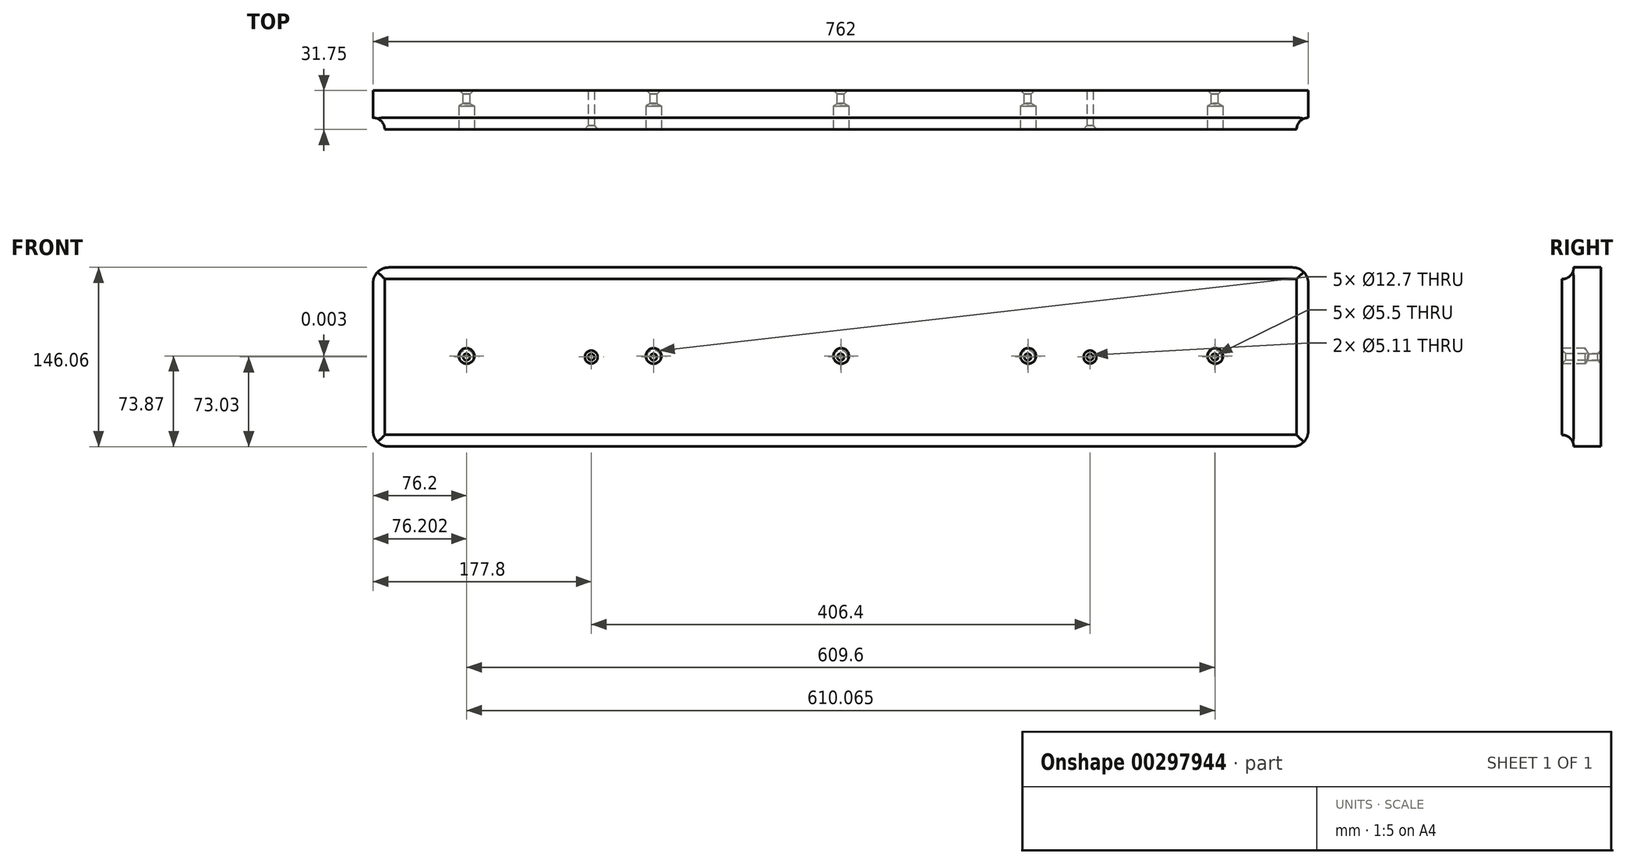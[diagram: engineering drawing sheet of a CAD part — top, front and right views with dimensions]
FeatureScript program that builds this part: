
annotation { "Feature Type Name" : "Feature", "Feature Type Description" : "" }
export const myFeature = defineFeature(function(context is Context, id is Id, definition is map)
    precondition{}
    {
        {
            var Q0;
            Q0=qCreatedBy(makeId("Front.planeOp"),FACE);
            var sketch = newSketch(context, id + "F0", { "sketchPlane" : qUnion([Q0])});
            skLineSegment(sketch, "E0.bottom", {"start": v(-381, 73.03) * mm, "end": v(381, 73.03) * mm});
            skLineSegment(sketch, "E0.top", {"start": v(-381, -73.03) * mm, "end": v(381, -73.03) * mm});
            skLineSegment(sketch, "E0.left", {"start": v(-381, 73.03) * mm, "end": v(-381, -73.03) * mm});
            skLineSegment(sketch, "E0.right", {"start": v(381, 73.03) * mm, "end": v(381, -73.03) * mm});
            skPoint(sketch, "E0.middle", {"position": v(0, 0) * mm});
            skLineSegment(sketch, "E1", {"start": v(0, 0) * mm, "end": v(152.4, 0) * mm, "construction": true});
            skLineSegment(sketch, "E2", {"start": v(152.4, 0) * mm, "end": v(304.8, 0) * mm, "construction": true});
            skLineSegment(sketch, "E3", {"start": v(0, 0) * mm, "end": v(-152.4, 0) * mm, "construction": true});
            skLineSegment(sketch, "E4", {"start": v(-152.4, 0) * mm, "end": v(-304.8, 0) * mm, "construction": true});
            skPoint(sketch, "E5", {"position": v(-304.8, 0) * mm});
            skPoint(sketch, "E6", {"position": v(-152.4, 0) * mm});
            skPoint(sketch, "E7", {"position": v(152.4, 0) * mm});
            skPoint(sketch, "E8", {"position": v(304.8, 0) * mm});
            skSolve(sketch);
        }
        {
            var Q0;
            Q0=qSketchRegion(id+"F0",true);
            extrude(context, id + "F1", {"entities" : qUnion([Q0]), "depth" : 31.75 * mm});
        }
        {
            var Q0;
            Q0=makeQuery(id+"F1.opExtrude","SWEPT_FACE",FACE,{"disambiguationData":[OSD([sQuery(id+"F0.wireOp",EDGE,"E0.left")])]});
            var sketch = newSketch(context, id + "F2", { "sketchPlane" : qUnion([Q0])});
            skCircle(sketch, "E9", {"center": v(31.75, 73.02) * mm, "radius": 9.53 * mm});
            skSolve(sketch);
        }
        {
            var Q0;
            Q0=qSketchRegion(id+"F2",true);
            extrude(context, id + "F3", {"entities" : qUnion([Q0]), "operationType" : NewBodyOperationType.REMOVE, "endBound" : BoundingType.THROUGH_ALL, "oppositeDirection" : true, "depth" : 25.4 * mm});
        }
        {
            var Q0;
            Q0=makeQuery(id+"F1.opExtrude","SWEPT_FACE",FACE,{"disambiguationData":[OSD([sQuery(id+"F0.wireOp",EDGE,"E0.bottom")])]});
            var sketch = newSketch(context, id + "F4", { "sketchPlane" : qUnion([Q0])});
            skCircle(sketch, "E10", {"center": v(-381, -31.73) * mm, "radius": 9.53 * mm});
            skSolve(sketch);
        }
        {
            var Q0;
            Q0=qSketchRegion(id+"F4",true);
            extrude(context, id + "F5", {"entities" : qUnion([Q0]), "operationType" : NewBodyOperationType.REMOVE, "endBound" : BoundingType.THROUGH_ALL, "oppositeDirection" : true, "depth" : 25.4 * mm});
        }
        {
            var Q0;
            Q0=makeQuery(id+"F1.opExtrude","SWEPT_FACE",FACE,{"disambiguationData":[OSD([sQuery(id+"F0.wireOp",EDGE,"E0.right")])]});
            var sketch = newSketch(context, id + "F6", { "sketchPlane" : qUnion([Q0])});
            skCircle(sketch, "E11", {"center": v(-31.75, -73.02) * mm, "radius": 9.53 * mm});
            skSolve(sketch);
        }
        {
            var Q0;
            Q0=qSketchRegion(id+"F6",true);
            extrude(context, id + "F7", {"entities" : qUnion([Q0]), "operationType" : NewBodyOperationType.REMOVE, "endBound" : BoundingType.THROUGH_ALL, "oppositeDirection" : true, "depth" : 25.4 * mm});
        }
        {
            var Q0;
            Q0=makeQuery(id+"F1.opExtrude","SWEPT_FACE",FACE,{"disambiguationData":[OSD([sQuery(id+"F0.wireOp",EDGE,"E0.top")])]});
            var sketch = newSketch(context, id + "F8", { "sketchPlane" : qUnion([Q0])});
            skCircle(sketch, "E12", {"center": v(381.03, 31.77) * mm, "radius": 9.52 * mm});
            skSolve(sketch);
        }
        {
            var Q0;
            Q0=qSketchRegion(id+"F8",true);
            extrude(context, id + "F9", {"entities" : qUnion([Q0]), "operationType" : NewBodyOperationType.REMOVE, "endBound" : BoundingType.THROUGH_ALL, "oppositeDirection" : true, "depth" : 25.4 * mm});
        }
        {
            var Q0;
            Q0=makeQuery(id+"F1.opExtrude","CAP_FACE",FACE,{"disambiguationData":[OSD([sQuery(id+"F0.wireOp",EDGE,"E0.bottom"),sQuery(id+"F0.wireOp",EDGE,"E0.top"),sQuery(id+"F0.wireOp",EDGE,"E0.left"),sQuery(id+"F0.wireOp",EDGE,"E0.right")])],"isStart":false});
            var sketch = newSketch(context, id + "F10", { "sketchPlane" : qUnion([Q0])});
            skLineSegment(sketch, "E13", {"start": v(0.47, 0.84) * mm, "end": v(152.87, 0.84) * mm, "construction": true});
            skLineSegment(sketch, "E14", {"start": v(152.87, 0.84) * mm, "end": v(305.27, 0.84) * mm, "construction": true});
            skLineSegment(sketch, "E15", {"start": v(-152.4, 0.84) * mm, "end": v(-304.8, 0.84) * mm, "construction": true});
            skLineSegment(sketch, "E16", {"start": v(0, 0) * mm, "end": v(-152.4, 0.84) * mm, "construction": true});
            skSolve(sketch);
        }
        {
            var Q0;
            Q0=sQuery(id+"F10.wireOp",VERTEX,"E15.end");
            var Q1;
            Q1=sQuery(id+"F10.wireOp",VERTEX,"E15.start");
            var Q2;
            Q2=sQuery(id+"F10.wireOp",VERTEX,"E13.start");
            var Q3;
            Q3=sQuery(id+"F10.wireOp",VERTEX,"E14.start");
            var Q4;
            Q4=sQuery(id+"F10.wireOp",VERTEX,"E14.end");
            var Q5;
            Q5=makeQuery(id+"F1.opExtrude","SWEPT_BODY",BODY,{"disambiguationData":[OSD([sQuery(id+"F0.wireOp",EDGE,"E0.bottom"),sQuery(id+"F0.wireOp",EDGE,"E0.top"),sQuery(id+"F0.wireOp",EDGE,"E0.left"),sQuery(id+"F0.wireOp",EDGE,"E0.right")])]});
            hole(context, id + "F11", {"style" : HoleStyle.SIMPLE, "endStyle" : HoleEndStyle.BLIND, "holeDiameter" : 12.7 * mm, "holeDepth" : 19.05 * mm, "tappedDepth" : 12.7 * mm, "tapClearance" : 3, "locations" : qUnion([Q0, Q1, Q2, Q3, Q4]), "scope" : qUnion([Q5])});
        }
        {
            var Q0;
            Q0=sQuery(id+"F0.wireOp",VERTEX,"E8");
            var Q1;
            Q1=sQuery(id+"F0.wireOp",VERTEX,"E7");
            var Q2;
            Q2=sQuery(id+"F0.wireOp",VERTEX,"E0.middle");
            var Q3;
            Q3=sQuery(id+"F0.wireOp",VERTEX,"E6");
            var Q4;
            Q4=sQuery(id+"F0.wireOp",VERTEX,"E5");
            var Q5;
            Q5=makeQuery(id+"F1.opExtrude","SWEPT_BODY",BODY,{"disambiguationData":[OSD([sQuery(id+"F0.wireOp",EDGE,"E0.bottom"),sQuery(id+"F0.wireOp",EDGE,"E0.top"),sQuery(id+"F0.wireOp",EDGE,"E0.left"),sQuery(id+"F0.wireOp",EDGE,"E0.right")])]});
            hole(context, id + "F12", {"style" : HoleStyle.C_SINK, "endStyle" : HoleEndStyle.THROUGH, "oppositeDirection" : true, "holeDiameter" : 5.5 * mm, "cSinkDiameter" : 11.2 * mm, "cSinkAngle" : 90 * degree, "tappedDepth" : 12.7 * mm, "tapClearance" : 3, "locations" : qUnion([Q0, Q1, Q2, Q3, Q4]), "scope" : qUnion([Q5])});
        }
        {
            var Q0;
            Q0=makeQuery(id+"F1.opExtrude","CAP_FACE",FACE,{"disambiguationData":[OSD([sQuery(id+"F0.wireOp",EDGE,"E0.bottom"),sQuery(id+"F0.wireOp",EDGE,"E0.top"),sQuery(id+"F0.wireOp",EDGE,"E0.left"),sQuery(id+"F0.wireOp",EDGE,"E0.right")])],"isStart":false});
            var sketch = newSketch(context, id + "F13", { "sketchPlane" : qUnion([Q0])});
            skLineSegment(sketch, "E17", {"start": v(0, 0) * mm, "end": v(-203.2, 0) * mm, "construction": true});
            skLineSegment(sketch, "E18", {"start": v(0, 0) * mm, "end": v(203.2, 0) * mm, "construction": true});
            skPoint(sketch, "E19", {"position": v(-203.2, 0) * mm});
            skPoint(sketch, "E20", {"position": v(203.2, 0) * mm});
            skSolve(sketch);
        }
        {
            var Q0;
            Q0=sQuery(id+"F13.wireOp",VERTEX,"E19");
            var Q1;
            Q1=sQuery(id+"F13.wireOp",VERTEX,"E18.end");
            var Q2;
            Q2=makeQuery(id+"F1.opExtrude","SWEPT_BODY",BODY,{"disambiguationData":[OSD([sQuery(id+"F0.wireOp",EDGE,"E0.bottom"),sQuery(id+"F0.wireOp",EDGE,"E0.top"),sQuery(id+"F0.wireOp",EDGE,"E0.left"),sQuery(id+"F0.wireOp",EDGE,"E0.right")])]});
            hole(context, id + "F14", {"style" : HoleStyle.C_SINK, "endStyle" : HoleEndStyle.THROUGH, "standardTappedOrClearance" : lookupTablePath({ "standard" : "ANSI", "fit" : "Normal (ASME)", "size" : "#10", "type" : "Clearance" }), "standardBlindInLast" : lookupTablePath({ "fit" : "Free", "standard" : "ANSI", "size" : "#10", "type" : "Clearance" }), "holeDiameter" : 5.1 * mm, "cSinkDiameter" : 10.44 * mm, "cSinkAngle" : 82 * degree, "tappedDepth" : 12.7 * mm, "tapClearance" : 3, "locations" : qUnion([Q0, Q1]), "scope" : qUnion([Q2])});
        }
        {
            var Q0;
            Q0=makeQuery(id+"F1.opExtrude","SWEPT_EDGE",EDGE,{"disambiguationData":[OSD([sQuery(id+"F0.wireOp",EDGE,"E0.bottom"),sQuery(id+"F0.wireOp",EDGE,"E0.right")])]});
            var Q1;
            Q1=makeQuery(id+"F1.opExtrude","SWEPT_EDGE",EDGE,{"disambiguationData":[OSD([sQuery(id+"F0.wireOp",EDGE,"E0.top"),sQuery(id+"F0.wireOp",EDGE,"E0.right")])]});
            var Q2;
            Q2=makeQuery(id+"F1.opExtrude","SWEPT_EDGE",EDGE,{"disambiguationData":[OSD([sQuery(id+"F0.wireOp",EDGE,"E0.bottom"),sQuery(id+"F0.wireOp",EDGE,"E0.left")])]});
            var Q3;
            Q3=makeQuery(id+"F1.opExtrude","SWEPT_EDGE",EDGE,{"disambiguationData":[OSD([sQuery(id+"F0.wireOp",EDGE,"E0.top"),sQuery(id+"F0.wireOp",EDGE,"E0.left")])]});
            fillet(context, id + "F15", {"entities" : qUnion([Q0, Q1, Q2, Q3]), "radius" : 12.7 * mm, "tangentPropagation" : true, "allowEdgeOverflow" : false});
        }
    });
